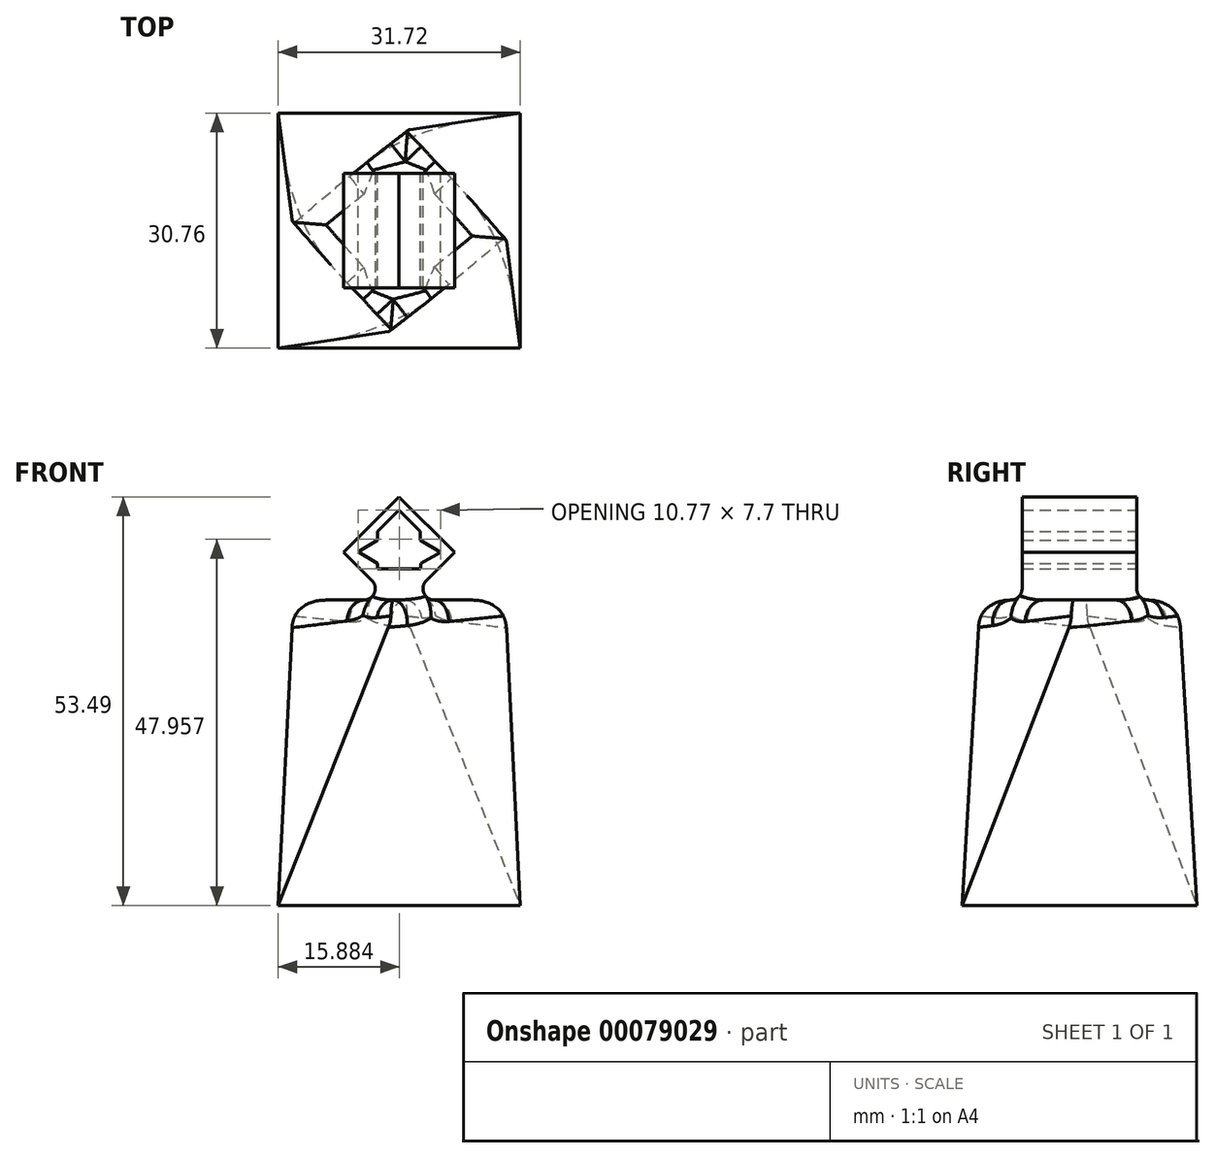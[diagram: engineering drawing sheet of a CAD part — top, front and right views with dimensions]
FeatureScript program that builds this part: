
annotation { "Feature Type Name" : "Feature", "Feature Type Description" : "" }
export const myFeature = defineFeature(function(context is Context, id is Id, definition is map)
    precondition{}
    {
        {
            var Q0;
            Q0=qCreatedBy(makeId("Top.planeOp"),FACE);
            var sketch = newSketch(context, id + "F0", { "sketchPlane" : qUnion([Q0])});
            skLineSegment(sketch, "E0.bottom", {"start": v(15.86, 15.38) * mm, "end": v(-15.86, 15.38) * mm});
            skLineSegment(sketch, "E0.top", {"start": v(15.86, -15.38) * mm, "end": v(-15.86, -15.38) * mm});
            skLineSegment(sketch, "E0.left", {"start": v(15.86, 15.38) * mm, "end": v(15.86, -15.38) * mm});
            skLineSegment(sketch, "E0.right", {"start": v(-15.86, 15.38) * mm, "end": v(-15.86, -15.38) * mm});
            skPoint(sketch, "E0.middle", {"position": v(0, 0) * mm});
            skSolve(sketch);
        }
        {
            var Q0;
            Q0=qCreatedBy(makeId("Top.planeOp"),FACE);
            cPlane(context, id + "F1", {"entities" : qUnion([Q0]), "cplaneType" : CPlaneType.OFFSET, "offset" : 40 * mm, "width" : 152.4 * mm, "height" : 152.4 * mm});
        }
        {
            var Q0;
            Q0=qCreatedBy(id+"F1.planeOp",FACE);
            var sketch = newSketch(context, id + "F2", { "sketchPlane" : qUnion([Q0])});
            skLineSegment(sketch, "E1", {"start": v(0, 13) * mm, "end": v(13.85, 0) * mm});
            skLineSegment(sketch, "E2", {"start": v(13.85, 0) * mm, "end": v(0, -13) * mm});
            skLineSegment(sketch, "E3", {"start": v(0, -13) * mm, "end": v(-13.85, 0) * mm});
            skLineSegment(sketch, "E4", {"start": v(-13.85, 0) * mm, "end": v(0, 13) * mm});
            skSolve(sketch);
        }
        {
            var Q0;
            Q0=makeQuery(id+"F2.imprint","IMPRINT",FACE,{"disambiguationData":[TD([[makeQuery(id+"F2.imprint","IMPRINT",EDGE,{"derivedFrom":sQuery(id+"F2.wireOp",EDGE,"E1")}),-1.0]])]});
            var Q1;
            Q1=makeQuery(id+"F0.imprint","IMPRINT",FACE,{"disambiguationData":[TD([[makeQuery(id+"F0.imprint","IMPRINT",EDGE,{"derivedFrom":sQuery(id+"F0.wireOp",EDGE,"E0.bottom")}),1.0]])]});
            loft(context, id + "F3", {"sheetProfilesArray" : [{ "sheetProfileEntities" : qUnion([Q0]) }, { "sheetProfileEntities" : qUnion([Q1]) }]});
        }
        {
            var Q0;
            Q0=qCreatedBy(makeId("Front.planeOp"),FACE);
            var sketch = newSketch(context, id + "F4", { "sketchPlane" : qUnion([Q0])});
            skLineSegment(sketch, "E5", {"start": v(0, 39) * mm, "end": v(7.25, 46.25) * mm});
            skLineSegment(sketch, "E6", {"start": v(7.25, 46.25) * mm, "end": v(0, 53.5) * mm});
            skLineSegment(sketch, "E7", {"start": v(0, 53.5) * mm, "end": v(-7.25, 46.25) * mm});
            skLineSegment(sketch, "E8", {"start": v(-7.25, 46.25) * mm, "end": v(0, 39) * mm});
            skLineSegment(sketch, "E9", {"start": v(7.25, 46.25) * mm, "end": v(-7.25, 46.25) * mm, "construction": true});
            skLineSegment(sketch, "E10", {"start": v(0, 53.5) * mm, "end": v(0, 39) * mm, "construction": true});
            skSolve(sketch);
        }
        {
            var Q0;
            Q0 = qSketchRegion(id + "F4", true);
            var Q1;
            Q1=makeQuery(id+"F4.imprint","IMPRINT",FACE,{"disambiguationData":[TD([[makeQuery(id+"F4.imprint","IMPRINT",EDGE,{"derivedFrom":sQuery(id+"F4.wireOp",EDGE,"E5")}),1.0]])]});
            extrude(context, id + "F5", {"entities" : qUnion([Q0, Q1]), "endBound" : BoundingType.SYMMETRIC, "depth" : 15 * mm});
        }
        {
            var Q0;
            Q0=makeQuery(id+"F5.opExtrude","CAP_FACE",FACE,{"disambiguationData":[OSD([sQuery(id+"F4.wireOp",EDGE,"E5"),sQuery(id+"F4.wireOp",EDGE,"E6"),sQuery(id+"F4.wireOp",EDGE,"E7"),sQuery(id+"F4.wireOp",EDGE,"E8")])],"isStart":true});
            var sketch = newSketch(context, id + "F6", { "sketchPlane" : qUnion([Q0])});
            skLineSegment(sketch, "E11", {"start": v(-2.75, 48.99) * mm, "end": v(2.82, 48.99) * mm});
            skLineSegment(sketch, "E12", {"start": v(2.82, 48.99) * mm, "end": v(2.82, 44.1) * mm});
            skLineSegment(sketch, "E13", {"start": v(2.82, 44.1) * mm, "end": v(-2.82, 44.1) * mm});
            skLineSegment(sketch, "E14", {"start": v(-2.82, 44.1) * mm, "end": v(-2.75, 48.99) * mm});
            skSolve(sketch);
        }
        {
            var Q0;
            Q0=makeQuery(id+"F6.imprint","IMPRINT",FACE,{"disambiguationData":[TD([[makeQuery(id+"F6.imprint","IMPRINT",EDGE,{"derivedFrom":sQuery(id+"F6.wireOp",EDGE,"E11")}),-1.0]])]});
            extrude(context, id + "F7", {"entities" : qUnion([Q0]), "operationType" : NewBodyOperationType.REMOVE, "oppositeDirection" : true, "depth" : 25 * mm});
        }
        {
            var Q0;
            Q0=makeQuery(id+"F5.opExtrude","CAP_FACE",FACE,{"disambiguationData":[OSD([sQuery(id+"F4.wireOp",EDGE,"E5"),sQuery(id+"F4.wireOp",EDGE,"E6"),sQuery(id+"F4.wireOp",EDGE,"E7"),sQuery(id+"F4.wireOp",EDGE,"E8")])],"isStart":true});
            var sketch = newSketch(context, id + "F8", { "sketchPlane" : qUnion([Q0])});
            skLineSegment(sketch, "E15", {"start": v(2.82, 48.99) * mm, "end": v(0.03, 51.8) * mm});
            skPoint(sketch, "E15.endSnap0", {"position": v(0.03, 48.99) * mm});
            skLineSegment(sketch, "E16", {"start": v(0.03, 51.8) * mm, "end": v(-2.75, 48.99) * mm});
            skSolve(sketch);
        }
        {
            var Q0;
            Q0=makeQuery(id+"F8.imprint","IMPRINT",FACE,{"disambiguationData":[TD([[makeQuery(id+"F8.imprint","IMPRINT",EDGE,{"derivedFrom":sQuery(id+"F8.wireOp",EDGE,"E15")}),1.0]])]});
            extrude(context, id + "F9", {"entities" : qUnion([Q0]), "operationType" : NewBodyOperationType.REMOVE, "oppositeDirection" : true, "depth" : 25 * mm});
        }
        {
            var Q0;
            Q0=makeQuery(id+"F5.opExtrude","CAP_FACE",FACE,{"disambiguationData":[OSD([sQuery(id+"F4.wireOp",EDGE,"E5"),sQuery(id+"F4.wireOp",EDGE,"E6"),sQuery(id+"F4.wireOp",EDGE,"E7"),sQuery(id+"F4.wireOp",EDGE,"E8")])],"isStart":true});
            var sketch = newSketch(context, id + "F10", { "sketchPlane" : qUnion([Q0])});
            skLineSegment(sketch, "E17", {"start": v(2.82, 47.82) * mm, "end": v(5.36, 46.3) * mm});
            skLineSegment(sketch, "E18", {"start": v(5.36, 46.3) * mm, "end": v(2.82, 44.8) * mm});
            skLineSegment(sketch, "E19", {"start": v(-2.77, 47.82) * mm, "end": v(-5.41, 46.25) * mm});
            skLineSegment(sketch, "E20", {"start": v(-2.8, 44.8) * mm, "end": v(-5.41, 46.25) * mm});
            skSolve(sketch);
        }
        {
            var Q0;
            {var subQ0=sQuery(id+"F10.wireOp",EDGE,"E17");Q0=makeQuery(id+"F10.imprint","IMPRINT",FACE,{"disambiguationData":[TD([[makeQuery(id+"F10.imprint","IMPRINT",EDGE,{"derivedFrom":subQ0}),-1.0]])]});}
            var Q1;
            {var subQ0=sQuery(id+"F10.wireOp",EDGE,"E19");Q1=makeQuery(id+"F10.imprint","IMPRINT",FACE,{"disambiguationData":[TD([[makeQuery(id+"F10.imprint","IMPRINT",EDGE,{"derivedFrom":subQ0}),1.0]])]});}
            extrude(context, id + "F11", {"entities" : qUnion([Q0, Q1]), "operationType" : NewBodyOperationType.REMOVE, "oppositeDirection" : true, "depth" : 25 * mm});
        }
        {
            var Q0;
            Q0=makeQuery(id+"F5.opExtrude","SWEPT_BODY",BODY,{"disambiguationData":[OSD([sQuery(id+"F4.wireOp",EDGE,"E5"),sQuery(id+"F4.wireOp",EDGE,"E6"),sQuery(id+"F4.wireOp",EDGE,"E7"),sQuery(id+"F4.wireOp",EDGE,"E8")])]});
            var Q1;
            Q1=makeQuery(id+"F3.opLoft","SWEPT_BODY",BODY,{"disambiguationData":[OSD([makeQuery(id+"F0.imprint","IMPRINT",FACE,{"disambiguationData":[TD([[makeQuery(id+"F0.imprint","IMPRINT",EDGE,{"derivedFrom":sQuery(id+"F0.wireOp",EDGE,"E0.bottom")}),1.0]])]}),makeQuery(id+"F2.imprint","IMPRINT",FACE,{"disambiguationData":[TD([[makeQuery(id+"F2.imprint","IMPRINT",EDGE,{"derivedFrom":sQuery(id+"F2.wireOp",EDGE,"E1")}),-1.0]])]})])]});
            booleanBodies(context, id + "F12", {"operationType" : BooleanOperationType.UNION, "tools" : qUnion([Q0, Q1])});
        }
        {
            var Q0;
            Q0=makeQuery(id+"F12.opBoolean","INTERSECT",EDGE,{"derivedFrom":[makeQuery(id+"F3.opLoft","CAP_FACE",FACE,{"disambiguationData":[OSD([makeQuery(id+"F2.imprint","IMPRINT",FACE,{"disambiguationData":[TD([[makeQuery(id+"F2.imprint","IMPRINT",EDGE,{"derivedFrom":sQuery(id+"F2.wireOp",EDGE,"E1")}),-1.0]])]})])],"isStart":true}),makeQuery(id+"F5.opExtrude","SWEPT_FACE",FACE,{"disambiguationData":[OSD([sQuery(id+"F4.wireOp",EDGE,"E8")])]})]});
            var Q1;
            Q1=makeQuery(id+"F12.opBoolean","INTERSECT",EDGE,{"derivedFrom":[makeQuery(id+"F3.opLoft","CAP_FACE",FACE,{"disambiguationData":[OSD([makeQuery(id+"F2.imprint","IMPRINT",FACE,{"disambiguationData":[TD([[makeQuery(id+"F2.imprint","IMPRINT",EDGE,{"derivedFrom":sQuery(id+"F2.wireOp",EDGE,"E1")}),-1.0]])]})])],"isStart":true}),makeQuery(id+"F5.opExtrude","SWEPT_FACE",FACE,{"disambiguationData":[OSD([sQuery(id+"F4.wireOp",EDGE,"E5")])]})]});
            var Q2;
            Q2=makeQuery(id+"F12.opBoolean","INTERSECT",EDGE,{"derivedFrom":[makeQuery(id+"F3.opLoft","CAP_FACE",FACE,{"disambiguationData":[OSD([makeQuery(id+"F2.imprint","IMPRINT",FACE,{"disambiguationData":[TD([[makeQuery(id+"F2.imprint","IMPRINT",EDGE,{"derivedFrom":sQuery(id+"F2.wireOp",EDGE,"E1")}),-1.0]])]})])],"isStart":true}),makeQuery(id+"F5.opExtrude","CAP_FACE",FACE,{"disambiguationData":[OSD([sQuery(id+"F4.wireOp",EDGE,"E5"),sQuery(id+"F4.wireOp",EDGE,"E6"),sQuery(id+"F4.wireOp",EDGE,"E7"),sQuery(id+"F4.wireOp",EDGE,"E8")])],"isStart":false})]});
            var Q3;
            Q3=makeQuery(id+"F12.opBoolean","INTERSECT",EDGE,{"derivedFrom":[makeQuery(id+"F3.opLoft","CAP_FACE",FACE,{"disambiguationData":[OSD([makeQuery(id+"F2.imprint","IMPRINT",FACE,{"disambiguationData":[TD([[makeQuery(id+"F2.imprint","IMPRINT",EDGE,{"derivedFrom":sQuery(id+"F2.wireOp",EDGE,"E1")}),-1.0]])]})])],"isStart":true}),makeQuery(id+"F5.opExtrude","CAP_FACE",FACE,{"disambiguationData":[OSD([sQuery(id+"F4.wireOp",EDGE,"E5"),sQuery(id+"F4.wireOp",EDGE,"E6"),sQuery(id+"F4.wireOp",EDGE,"E7"),sQuery(id+"F4.wireOp",EDGE,"E8")])],"isStart":true})]});
            fillet(context, id + "F13", {"entities" : qUnion([Q0, Q1, Q2, Q3]), "radius" : 1.5 * mm, "tangentPropagation" : true, "allowEdgeOverflow" : false});
        }
        {
            var Q0;
            Q0=makeQuery(id+"F3.opLoft","MID_CAP_EDGE",EDGE,{"disambiguationData":[OSD([sQuery(id+"F2.wireOp",EDGE,"E2"),sQuery(id+"F2.wireOp",EDGE,"E3"),sQuery(id+"F2.wireOp",EDGE,"E4")])],"capPos":0.0});
            var Q1;
            Q1=makeQuery(id+"F3.opLoft","MID_CAP_EDGE",EDGE,{"disambiguationData":[OSD([sQuery(id+"F2.wireOp",EDGE,"E1"),sQuery(id+"F2.wireOp",EDGE,"E2"),sQuery(id+"F2.wireOp",EDGE,"E3")])],"capPos":0.0});
            var Q2;
            Q2=makeQuery(id+"F3.opLoft","MID_CAP_EDGE",EDGE,{"disambiguationData":[OSD([sQuery(id+"F2.wireOp",EDGE,"E1"),sQuery(id+"F2.wireOp",EDGE,"E2"),sQuery(id+"F2.wireOp",EDGE,"E4")])],"capPos":0.0});
            var Q3;
            Q3=makeQuery(id+"F3.opLoft","MID_CAP_EDGE",EDGE,{"disambiguationData":[OSD([sQuery(id+"F2.wireOp",EDGE,"E1"),sQuery(id+"F2.wireOp",EDGE,"E3"),sQuery(id+"F2.wireOp",EDGE,"E4")])],"capPos":0.0});
            fillet(context, id + "F14", {"entities" : qUnion([Q0, Q1, Q2, Q3]), "radius" : 3 * mm, "tangentPropagation" : true, "allowEdgeOverflow" : false});
        }
    });
